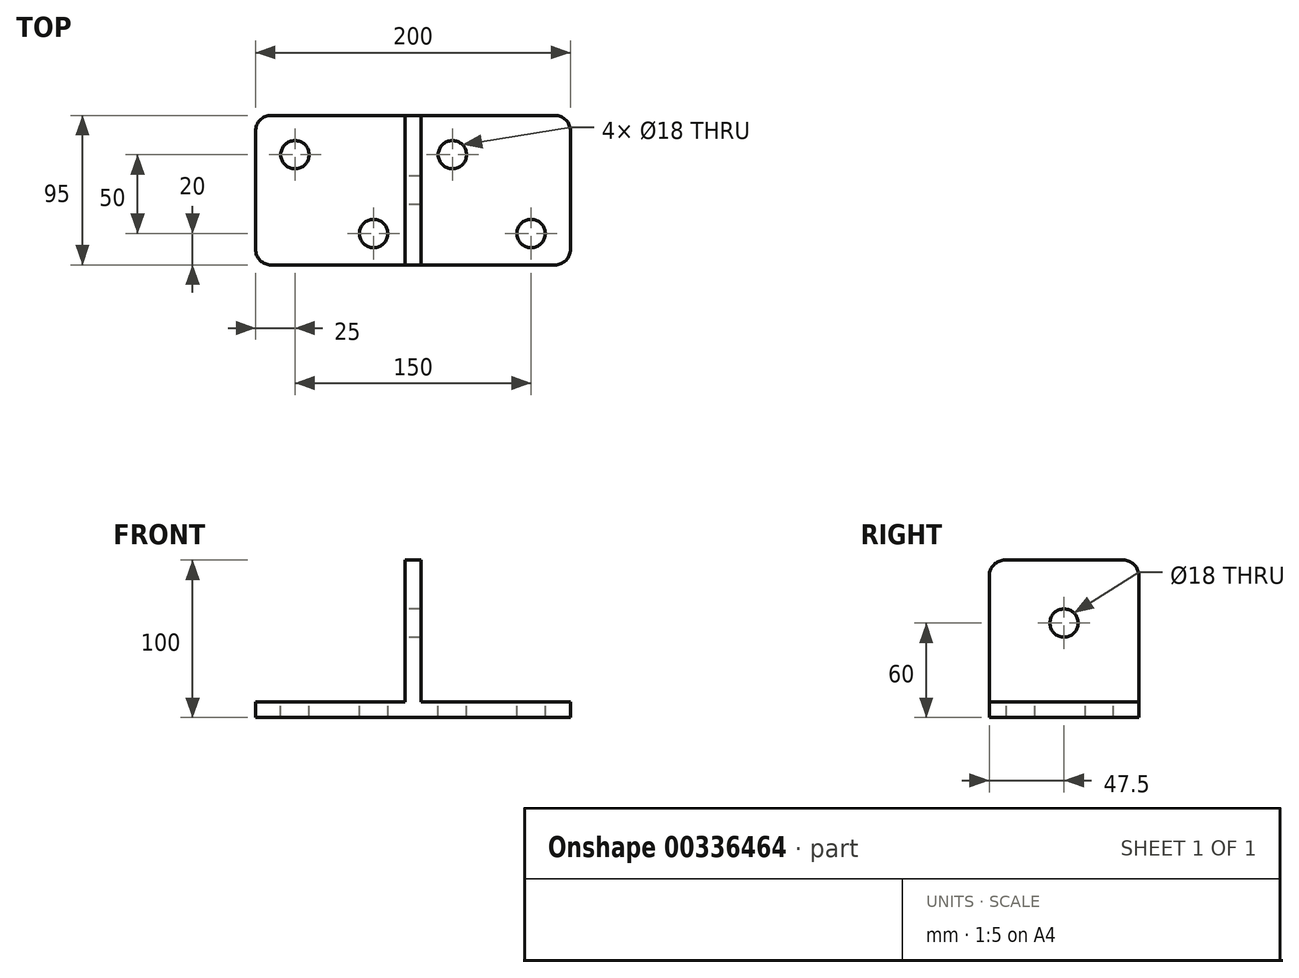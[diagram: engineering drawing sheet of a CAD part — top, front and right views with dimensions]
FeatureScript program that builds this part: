
annotation { "Feature Type Name" : "Feature", "Feature Type Description" : "" }
export const myFeature = defineFeature(function(context is Context, id is Id, definition is map)
    precondition{}
    {
        {
            var Q0;
            Q0=qCreatedBy(makeId("Front.planeOp"),FACE);
            var sketch = newSketch(context, id + "F0", { "sketchPlane" : qUnion([Q0])});
            skLineSegment(sketch, "E0", {"start": v(0, 0) * mm, "end": v(100, 0) * mm});
            skLineSegment(sketch, "E1", {"start": v(100, 0) * mm, "end": v(100, 10) * mm});
            skLineSegment(sketch, "E2", {"start": v(100, 10) * mm, "end": v(5, 10) * mm});
            skLineSegment(sketch, "E3", {"start": v(5, 10) * mm, "end": v(5, 100) * mm});
            skLineSegment(sketch, "E4", {"start": v(5, 100) * mm, "end": v(0, 100) * mm});
            skLineSegment(sketch, "E5.MirrorCS", {"start": v(-5, 100) * mm, "end": v(0, 100) * mm});
            skLineSegment(sketch, "E6.MirrorCS", {"start": v(-100, 0) * mm, "end": v(-100, 10) * mm});
            skLineSegment(sketch, "E7.MirrorCS", {"start": v(-100, 10) * mm, "end": v(-5, 10) * mm});
            skLineSegment(sketch, "E8.MirrorCS", {"start": v(0, 0) * mm, "end": v(-100, 0) * mm});
            skLineSegment(sketch, "E9.MirrorCS", {"start": v(-5, 10) * mm, "end": v(-5, 100) * mm});
            skSolve(sketch);
        }
        {
            var Q0;
            Q0=makeQuery(id+"F0.imprint","IMPRINT",FACE,{"disambiguationData":[TD([[makeQuery(id+"F0.imprint","IMPRINT",EDGE,{"derivedFrom":sQuery(id+"F0.wireOp",EDGE,"E0")}),1.0]])]});
            extrude(context, id + "F1", {"entities" : qUnion([Q0]), "endBound" : BoundingType.SYMMETRIC, "depth" : 95 * mm});
        }
        {
            var Q0;
            Q0=makeQuery(id+"F1.opExtrude","SWEPT_FACE",FACE,{"disambiguationData":[OSD([sQuery(id+"F0.wireOp",EDGE,"E2")])]});
            var sketch = newSketch(context, id + "F2", { "sketchPlane" : qUnion([Q0])});
            skCircle(sketch, "E10", {"center": v(75, -27.5) * mm, "radius": 9 * mm});
            skCircle(sketch, "E11", {"center": v(25, 22.5) * mm, "radius": 9 * mm});
            skCircle(sketch, "E12.MirrorC", {"center": v(-25, -27.5) * mm, "radius": 9 * mm});
            skCircle(sketch, "E13.MirrorC", {"center": v(-75, 22.5) * mm, "radius": 9 * mm});
            skSolve(sketch);
        }
        {
            var Q0;
            Q0 = qSketchRegion(id + "F2", true);
            extrude(context, id + "F3", {"entities" : qUnion([Q0]), "operationType" : NewBodyOperationType.REMOVE, "oppositeDirection" : true, "depth" : 25 * mm});
        }
        {
            var Q0;
            Q0=makeQuery(id+"F1.opExtrude","SWEPT_FACE",FACE,{"disambiguationData":[OSD([sQuery(id+"F0.wireOp",EDGE,"E9.MirrorCS")])]});
            var sketch = newSketch(context, id + "F4", { "sketchPlane" : qUnion([Q0])});
            skCircle(sketch, "E14", {"center": v(0, 60) * mm, "radius": 9 * mm});
            skSolve(sketch);
        }
        {
            var Q0;
            Q0 = qSketchRegion(id + "F4", true);
            extrude(context, id + "F5", {"entities" : qUnion([Q0]), "operationType" : NewBodyOperationType.REMOVE, "oppositeDirection" : true, "depth" : 25 * mm});
        }
        {
            var Q0;
            Q0=makeQuery(id+"F1.opExtrude","CAP_EDGE",EDGE,{"disambiguationData":[OSD([sQuery(id+"F0.wireOp",EDGE,"E1")])],"isStart":false});
            var Q1;
            Q1=makeQuery(id+"F1.opExtrude","CAP_EDGE",EDGE,{"disambiguationData":[OSD([sQuery(id+"F0.wireOp",EDGE,"E1")])],"isStart":true});
            var Q2;
            Q2=makeQuery(id+"F1.opExtrude","CAP_EDGE",EDGE,{"disambiguationData":[OSD([sQuery(id+"F0.wireOp",EDGE,"E4"),sQuery(id+"F0.wireOp",EDGE,"E5.MirrorCS")])],"isStart":true});
            var Q3;
            Q3=makeQuery(id+"F1.opExtrude","CAP_EDGE",EDGE,{"disambiguationData":[OSD([sQuery(id+"F0.wireOp",EDGE,"E4"),sQuery(id+"F0.wireOp",EDGE,"E5.MirrorCS")])],"isStart":false});
            var Q4;
            Q4=makeQuery(id+"F1.opExtrude","CAP_EDGE",EDGE,{"disambiguationData":[OSD([sQuery(id+"F0.wireOp",EDGE,"E6.MirrorCS")])],"isStart":false});
            var Q5;
            Q5=makeQuery(id+"F1.opExtrude","CAP_EDGE",EDGE,{"disambiguationData":[OSD([sQuery(id+"F0.wireOp",EDGE,"E6.MirrorCS")])],"isStart":true});
            fillet(context, id + "F6", {"entities" : qUnion([Q0, Q1, Q2, Q3, Q4, Q5]), "radius" : 10 * mm, "tangentPropagation" : true, "allowEdgeOverflow" : false});
        }
    });
